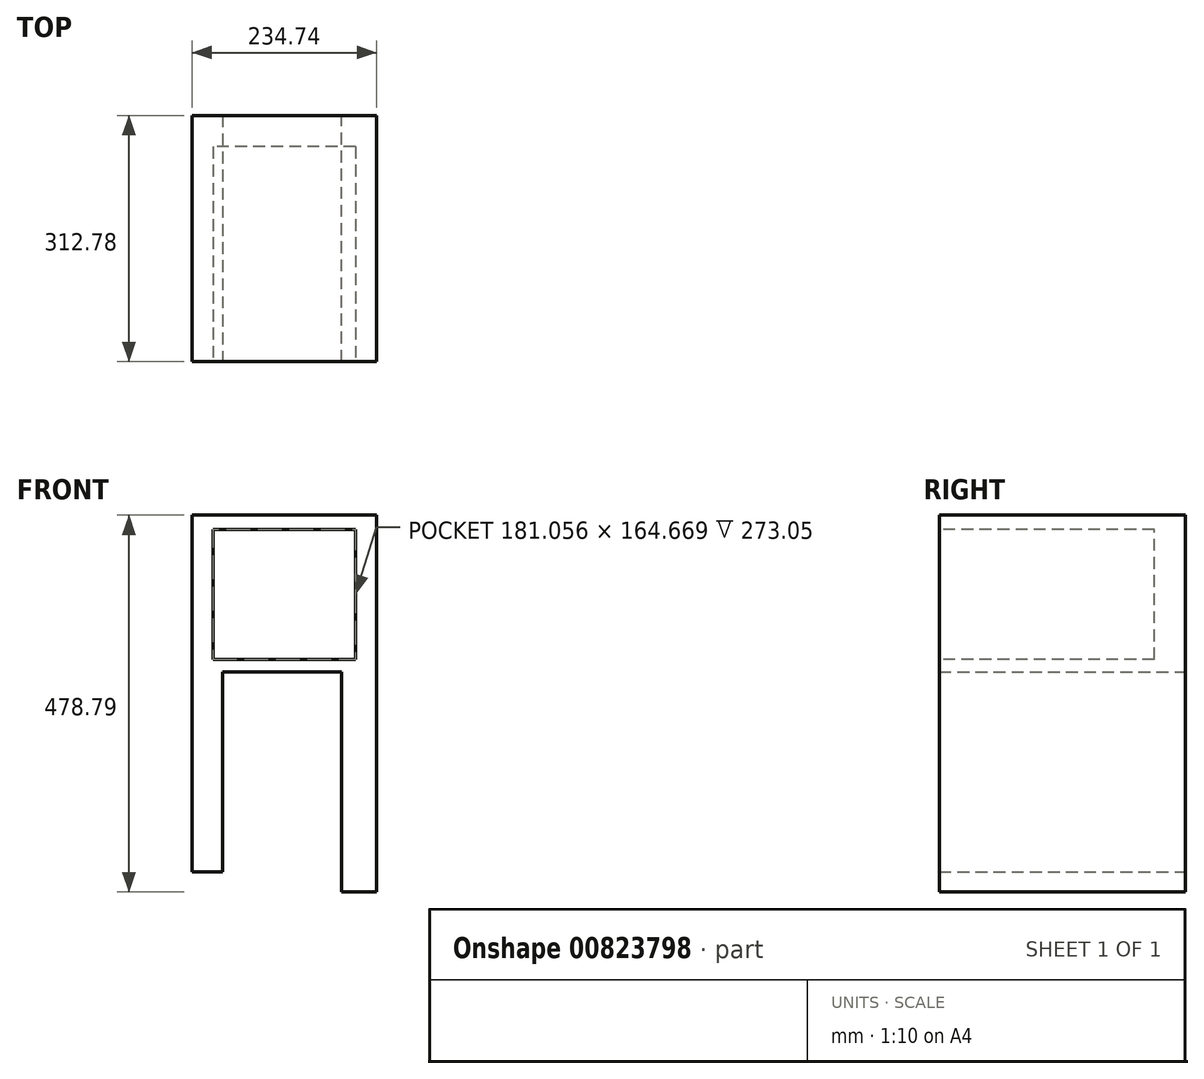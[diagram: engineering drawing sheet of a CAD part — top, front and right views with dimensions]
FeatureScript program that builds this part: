
annotation { "Feature Type Name" : "Feature", "Feature Type Description" : "" }
export const myFeature = defineFeature(function(context is Context, id is Id, definition is map)
    precondition{}
    {
        {
            var Q0;
            Q0=qCreatedBy(makeId("Top.planeOp"),FACE);
            var sketch = newSketch(context, id + "F0", { "sketchPlane" : qUnion([Q0])});
            skLineSegment(sketch, "E0.bottom", {"start": v(117.37, -156.4) * mm, "end": v(-117.37, -156.4) * mm});
            skLineSegment(sketch, "E0.top", {"start": v(117.37, 156.4) * mm, "end": v(-117.37, 156.4) * mm});
            skLineSegment(sketch, "E0.left", {"start": v(117.37, -156.4) * mm, "end": v(117.37, 156.4) * mm});
            skLineSegment(sketch, "E0.right", {"start": v(-117.37, -156.4) * mm, "end": v(-117.37, 156.4) * mm});
            skPoint(sketch, "E0.middle", {"position": v(0, 0) * mm});
            skSolve(sketch);
        }
        {
            var Q0;
            Q0 = qSketchRegion(id + "F0", true);
            extrude(context, id + "F1", {"entities" : qUnion([Q0]), "depth" : 199.39 * mm, "offsetDistance" : 25.4 * mm});
        }
        {
            var Q0;
            Q0=makeQuery(id+"F1.opExtrude","SWEPT_FACE",FACE,{"disambiguationData":[OSD([sQuery(id+"F0.wireOp",EDGE,"E0.bottom")])]});
            var sketch = newSketch(context, id + "F2", { "sketchPlane" : qUnion([Q0])});
            skLineSegment(sketch, "E1.bottom", {"start": v(92.1, 14.54) * mm, "end": v(-92.1, 14.54) * mm});
            skLineSegment(sketch, "E1.top", {"start": v(92.1, 158.12) * mm, "end": v(-92.1, 158.12) * mm});
            skLineSegment(sketch, "E1.left", {"start": v(92.1, 14.54) * mm, "end": v(92.1, 158.12) * mm});
            skLineSegment(sketch, "E1.right", {"start": v(-92.1, 14.54) * mm, "end": v(-92.1, 158.12) * mm});
            skPoint(sketch, "E1.middle", {"position": v(0, 86.33) * mm});
            skSolve(sketch);
        }
        {
            var Q0;
            Q0 = qSketchRegion(id + "F2", true);
            extrude(context, id + "F3", {"entities" : qUnion([Q0]), "operationType" : NewBodyOperationType.ADD, "oppositeDirection" : true, "depth" : 283.46 * mm, "offsetDistance" : 25.4 * mm});
        }
        {
            var Q0;
            Q0=makeQuery(id+"F1.opExtrude","SWEPT_FACE",FACE,{"disambiguationData":[OSD([sQuery(id+"F0.wireOp",EDGE,"E0.bottom")])]});
            var sketch = newSketch(context, id + "F4", { "sketchPlane" : qUnion([Q0])});
            skLineSegment(sketch, "E2.bottom", {"start": v(90.65, 24.27) * mm, "end": v(-90.65, 24.27) * mm});
            skLineSegment(sketch, "E2.top", {"start": v(90.65, 164.94) * mm, "end": v(-90.65, 164.94) * mm});
            skLineSegment(sketch, "E2.left", {"start": v(90.65, 24.27) * mm, "end": v(90.65, 164.94) * mm});
            skLineSegment(sketch, "E2.right", {"start": v(-90.65, 24.27) * mm, "end": v(-90.65, 164.94) * mm});
            skPoint(sketch, "E2.middle", {"position": v(0, 94.6) * mm});
            skSolve(sketch);
        }
        {
            var Q0;
            Q0=makeQuery(id+"F4.imprint","IMPRINT",FACE,{"disambiguationData":[TD([[makeQuery(id+"F4.imprint","IMPRINT",EDGE,{"derivedFrom":sQuery(id+"F4.wireOp",EDGE,"E2.bottom")}),-1.0]])]});
            extrude(context, id + "F5", {"entities" : qUnion([Q0]), "operationType" : NewBodyOperationType.ADD, "oppositeDirection" : true, "depth" : 248.16 * mm, "offsetDistance" : 25.4 * mm});
        }
        {
            var Q0;
            Q0 = qSketchRegion(id + "F4", true);
            extrude(context, id + "F6", {"entities" : qUnion([Q0]), "operationType" : NewBodyOperationType.ADD, "oppositeDirection" : true, "depth" : 270 * mm, "offsetDistance" : 25.4 * mm});
        }
        {
            var Q0;
            Q0=makeQuery(id+"F1.opExtrude","SWEPT_FACE",FACE,{"disambiguationData":[OSD([sQuery(id+"F0.wireOp",EDGE,"E0.bottom")])]});
            var sketch = newSketch(context, id + "F7", { "sketchPlane" : qUnion([Q0])});
            skLineSegment(sketch, "E3.bottom", {"start": v(90.53, 16.23) * mm, "end": v(-90.53, 16.23) * mm});
            skLineSegment(sketch, "E3.top", {"start": v(90.53, 180.9) * mm, "end": v(-90.53, 180.9) * mm});
            skLineSegment(sketch, "E3.left", {"start": v(90.53, 16.23) * mm, "end": v(90.53, 180.9) * mm});
            skLineSegment(sketch, "E3.right", {"start": v(-90.53, 16.23) * mm, "end": v(-90.53, 180.9) * mm});
            skPoint(sketch, "E3.middle", {"position": v(0, 98.57) * mm});
            skSolve(sketch);
        }
        {
            var Q0;
            Q0=makeQuery(id+"F7.imprint","IMPRINT",FACE,{"disambiguationData":[TD([[makeQuery(id+"F7.imprint","IMPRINT",EDGE,{"derivedFrom":sQuery(id+"F7.wireOp",EDGE,"E3.bottom")}),-1.0]])]});
            extrude(context, id + "F8", {"entities" : qUnion([Q0]), "operationType" : NewBodyOperationType.REMOVE, "oppositeDirection" : true, "depth" : 273.05 * mm, "offsetDistance" : 25.4 * mm});
        }
        {
            var Q0;
            Q0=makeQuery(id+"F1.opExtrude","CAP_FACE",FACE,{"disambiguationData":[OSD([sQuery(id+"F0.wireOp",EDGE,"E0.bottom"),sQuery(id+"F0.wireOp",EDGE,"E0.top"),sQuery(id+"F0.wireOp",EDGE,"E0.left"),sQuery(id+"F0.wireOp",EDGE,"E0.right")])],"isStart":true});
            var sketch = newSketch(context, id + "F9", { "sketchPlane" : qUnion([Q0])});
            skLineSegment(sketch, "E4.bottom", {"start": v(78.6, -125.6) * mm, "end": v(-78.6, -125.6) * mm});
            skLineSegment(sketch, "E4.top", {"start": v(78.6, 125.6) * mm, "end": v(-78.6, 125.6) * mm});
            skLineSegment(sketch, "E4.left", {"start": v(78.6, -125.6) * mm, "end": v(78.6, 125.6) * mm});
            skLineSegment(sketch, "E4.right", {"start": v(-78.6, -125.6) * mm, "end": v(-78.6, 125.6) * mm});
            skPoint(sketch, "E4.middle", {"position": v(0, 0) * mm});
            skLineSegment(sketch, "E5.bottom", {"start": v(-78.6, 125.6) * mm, "end": v(79, 125.6) * mm});
            skLineSegment(sketch, "E5.top", {"start": v(-78.6, 156.4) * mm, "end": v(79, 156.4) * mm});
            skLineSegment(sketch, "E5.left", {"start": v(-78.6, 125.6) * mm, "end": v(-78.6, 156.4) * mm});
            skLineSegment(sketch, "E5.right", {"start": v(79, 125.6) * mm, "end": v(79, 156.4) * mm});
            skLineSegment(sketch, "E6.top", {"start": v(78.6, -156.4) * mm, "end": v(-78.6, -156.4) * mm});
            skLineSegment(sketch, "E6.left", {"start": v(78.6, -125.6) * mm, "end": v(78.6, -156.4) * mm});
            skLineSegment(sketch, "E6.right", {"start": v(-78.6, -125.6) * mm, "end": v(-78.6, -156.4) * mm});
            skSolve(sketch);
        }
        {
            var Q0;
            Q0=makeQuery(id+"F9.imprint","IMPRINT",FACE,{"disambiguationData":[TD([[makeQuery(id+"F9.imprint","IMPRINT",EDGE,{"derivedFrom":sQuery(id+"F9.wireOp",EDGE,"E4.right")}),1.0]])]});
            extrude(context, id + "F10", {"entities" : qUnion([Q0]), "operationType" : NewBodyOperationType.ADD, "depth" : 254 * mm, "offsetDistance" : 25.4 * mm});
        }
        {
            var Q0;
            Q0=makeQuery(id+"F1.opExtrude","CAP_FACE",FACE,{"disambiguationData":[OSD([sQuery(id+"F0.wireOp",EDGE,"E0.bottom"),sQuery(id+"F0.wireOp",EDGE,"E0.top"),sQuery(id+"F0.wireOp",EDGE,"E0.left"),sQuery(id+"F0.wireOp",EDGE,"E0.right")])],"isStart":true});
            var sketch = newSketch(context, id + "F11", { "sketchPlane" : qUnion([Q0])});
            skLineSegment(sketch, "E7.bottom", {"start": v(117.37, 156.4) * mm, "end": v(72.8, 156.4) * mm});
            skLineSegment(sketch, "E7.top", {"start": v(117.37, -156.4) * mm, "end": v(72.8, -156.4) * mm});
            skLineSegment(sketch, "E7.left", {"start": v(117.37, 156.4) * mm, "end": v(117.37, -156.4) * mm});
            skLineSegment(sketch, "E7.right", {"start": v(72.8, 156.4) * mm, "end": v(72.8, -156.4) * mm});
            skSolve(sketch);
        }
        {
            var Q0;
            Q0=makeQuery(id+"F11.imprint","IMPRINT",FACE,{"disambiguationData":[TD([[makeQuery(id+"F11.imprint","IMPRINT",EDGE,{"derivedFrom":sQuery(id+"F11.wireOp",EDGE,"E7.bottom")}),1.0]])]});
            extrude(context, id + "F12", {"entities" : qUnion([Q0]), "operationType" : NewBodyOperationType.ADD, "depth" : 25.4 * mm, "offsetDistance" : 25.4 * mm});
        }
        {
            var Q0;
            Q0=makeQuery(id+"F12.opExtrude","CAP_FACE",FACE,{"disambiguationData":[OSD([sQuery(id+"F11.wireOp",EDGE,"E7.bottom"),sQuery(id+"F11.wireOp",EDGE,"E7.top"),sQuery(id+"F11.wireOp",EDGE,"E7.left"),sQuery(id+"F11.wireOp",EDGE,"E7.right")])],"isStart":false});
            extrude(context, id + "F13", {"entities" : qUnion([Q0]), "operationType" : NewBodyOperationType.ADD, "depth" : 254 * mm, "offsetDistance" : 25.4 * mm});
        }
    });
